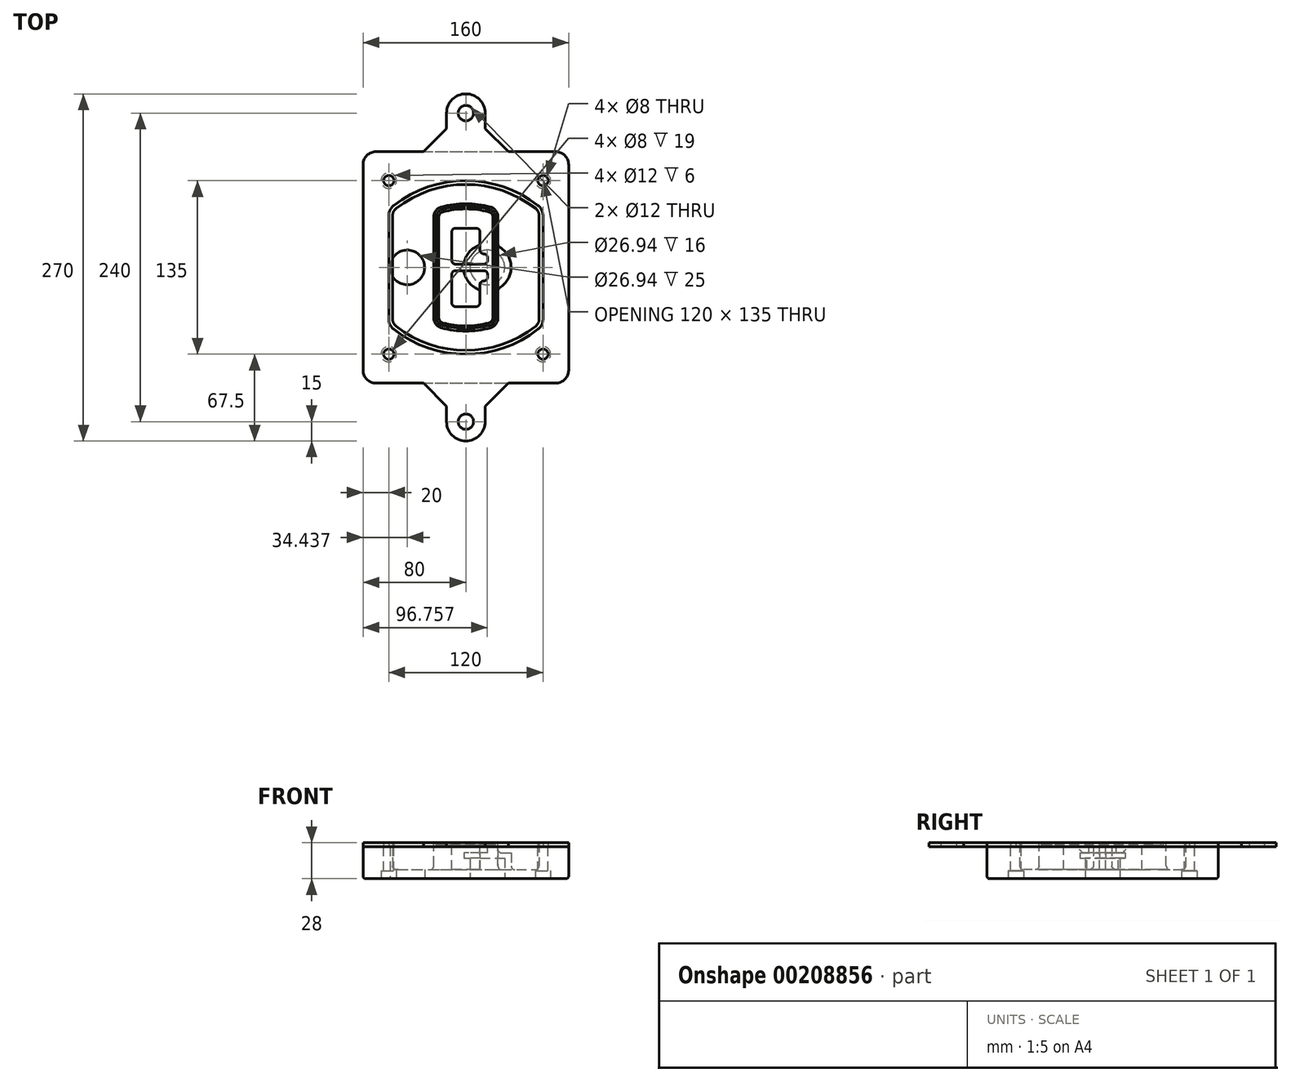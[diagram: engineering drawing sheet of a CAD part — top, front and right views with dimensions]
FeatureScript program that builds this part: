
annotation { "Feature Type Name" : "Feature", "Feature Type Description" : "" }
export const myFeature = defineFeature(function(context is Context, id is Id, definition is map)
    precondition{}
    {
        {
            var Q0;
            Q0=qCreatedBy(makeId("Top.planeOp"),FACE);
            var sketch = newSketch(context, id + "F0", { "sketchPlane" : qUnion([Q0])});
            skPoint(sketch, "E0.rect.middle", {"position": v(0, 0) * mm});
            skLineSegment(sketch, "E1.bottom", {"start": v(-70, -90) * mm, "end": v(70, -90) * mm});
            skLineSegment(sketch, "E1.top", {"start": v(-70, 90) * mm, "end": v(70, 90) * mm});
            skLineSegment(sketch, "E1.left", {"start": v(-80, -80) * mm, "end": v(-80, 80) * mm});
            skLineSegment(sketch, "E1.right", {"start": v(80, -80) * mm, "end": v(80, 80) * mm});
            skLineSegment(sketch, "E2", {"start": v(-80, 90) * mm, "end": v(80, -90) * mm, "construction": true});
            skLineSegment(sketch, "E3", {"start": v(80, 90) * mm, "end": v(-80, -90) * mm, "construction": true});
            skCircle(sketch, "E4", {"center": v(-60, 67.5) * mm, "radius": 4 * mm});
            skCircle(sketch, "E5", {"center": v(60, 67.5) * mm, "radius": 4 * mm});
            skCircle(sketch, "E6", {"center": v(60, -67.5) * mm, "radius": 4 * mm});
            skCircle(sketch, "E7", {"center": v(-60, -67.5) * mm, "radius": 4 * mm});
            skLineSegment(sketch, "E8", {"start": v(-60, 67.5) * mm, "end": v(60, 67.5) * mm, "construction": true});
            skLineSegment(sketch, "E9", {"start": v(60, 67.5) * mm, "end": v(60, -67.5) * mm, "construction": true});
            skLineSegment(sketch, "E10", {"start": v(60, -67.5) * mm, "end": v(-60, -67.5) * mm, "construction": true});
            skLineSegment(sketch, "E11", {"start": v(-60, -67.5) * mm, "end": v(-60, 67.5) * mm, "construction": true});
            skLineSegment(sketch, "E12", {"start": v(-60, 40.3) * mm, "end": v(-60, -40.3) * mm});
            skLineSegment(sketch, "E13", {"start": v(60, 40.3) * mm, "end": v(60, -40.3) * mm});
            skArc(sketch, "E14", {"start": v(56.15, 48.18) * mm, "mid": v(0, 67.5) * mm, "end": v(-56.15, 48.18) * mm});
            skArc(sketch, "E15", {"start": v(-56.15, -48.18) * mm, "mid": v(0, -67.5) * mm, "end": v(56.15, -48.18) * mm});
            skLineSegment(sketch, "E16", {"start": v(-60, 0) * mm, "end": v(60, 0) * mm, "construction": true});
            skPoint(sketch, "E17.visualSharp", {"position": v(-60, -45) * mm});
            skArc(sketch, "E17.filletArc", {"start": v(-60, -40.3) * mm, "mid": v(-58.99, -44.68) * mm, "end": v(-56.15, -48.18) * mm});
            skPoint(sketch, "E18.visualSharp", {"position": v(-60, 45) * mm});
            skArc(sketch, "E18.filletArc", {"start": v(-56.15, 48.18) * mm, "mid": v(-58.99, 44.68) * mm, "end": v(-60, 40.3) * mm});
            skPoint(sketch, "E19.visualSharp", {"position": v(60, 45) * mm});
            skArc(sketch, "E19.filletArc", {"start": v(60, 40.3) * mm, "mid": v(58.99, 44.68) * mm, "end": v(56.15, 48.18) * mm});
            skPoint(sketch, "E20.visualSharp", {"position": v(60, -45) * mm});
            skArc(sketch, "E20.filletArc", {"start": v(56.15, -48.18) * mm, "mid": v(58.99, -44.68) * mm, "end": v(60, -40.3) * mm});
            skPoint(sketch, "E21.visualSharp", {"position": v(-80, 90) * mm});
            skArc(sketch, "E21.filletArc", {"start": v(-70, 90) * mm, "mid": v(-77.07, 87.07) * mm, "end": v(-80, 80) * mm});
            skPoint(sketch, "E22.visualSharp", {"position": v(80, 90) * mm});
            skArc(sketch, "E22.filletArc", {"start": v(80, 80) * mm, "mid": v(77.07, 87.07) * mm, "end": v(70, 90) * mm});
            skPoint(sketch, "E23.visualSharp", {"position": v(80, -90) * mm});
            skArc(sketch, "E23.filletArc", {"start": v(70, -90) * mm, "mid": v(77.07, -87.07) * mm, "end": v(80, -80) * mm});
            skPoint(sketch, "E24.visualSharp", {"position": v(-80, -90) * mm});
            skArc(sketch, "E24.filletArc", {"start": v(-80, -80) * mm, "mid": v(-77.07, -87.07) * mm, "end": v(-70, -90) * mm});
            skArc(sketch, "E25.0", {"start": v(57, 40.3) * mm, "mid": v(56.3, 43.36) * mm, "end": v(54.3, 45.81) * mm});
            skLineSegment(sketch, "E25.1", {"start": v(57, 40.3) * mm, "end": v(57, -40.3) * mm});
            skArc(sketch, "E25.2", {"start": v(54.3, -45.81) * mm, "mid": v(56.3, -43.36) * mm, "end": v(57, -40.3) * mm});
            skArc(sketch, "E25.3", {"start": v(-54.3, -45.81) * mm, "mid": v(0, -64.5) * mm, "end": v(54.3, -45.81) * mm});
            skArc(sketch, "E25.4", {"start": v(-57, -40.3) * mm, "mid": v(-56.3, -43.36) * mm, "end": v(-54.3, -45.81) * mm});
            skArc(sketch, "E25.5", {"start": v(54.3, 45.81) * mm, "mid": v(0, 64.5) * mm, "end": v(-54.3, 45.81) * mm});
            skLineSegment(sketch, "E25.6", {"start": v(-57, 40.3) * mm, "end": v(-57, -40.3) * mm});
            skArc(sketch, "E25.7", {"start": v(-54.3, 45.81) * mm, "mid": v(-56.3, 43.36) * mm, "end": v(-57, 40.3) * mm});
            skArc(sketch, "E26.0", {"start": v(-58.62, 51.33) * mm, "mid": v(-62.58, 46.43) * mm, "end": v(-64, 40.3) * mm});
            skArc(sketch, "E26.1", {"start": v(58.62, 51.33) * mm, "mid": v(0, 71.5) * mm, "end": v(-58.62, 51.33) * mm});
            skArc(sketch, "E26.2", {"start": v(64, 40.3) * mm, "mid": v(62.58, 46.43) * mm, "end": v(58.62, 51.33) * mm});
            skLineSegment(sketch, "E26.3", {"start": v(64, 40.3) * mm, "end": v(64, -40.3) * mm});
            skArc(sketch, "E26.4", {"start": v(58.62, -51.33) * mm, "mid": v(62.58, -46.43) * mm, "end": v(64, -40.3) * mm});
            skLineSegment(sketch, "E26.5", {"start": v(-64, 40.3) * mm, "end": v(-64, -40.3) * mm});
            skArc(sketch, "E26.6", {"start": v(-58.62, -51.33) * mm, "mid": v(0, -71.5) * mm, "end": v(58.62, -51.33) * mm});
            skArc(sketch, "E26.7", {"start": v(-64, -40.3) * mm, "mid": v(-62.58, -46.43) * mm, "end": v(-58.62, -51.33) * mm});
            skSolve(sketch);
        }
        {
            var Q0;
            Q0=makeQuery(id+"F0.imprint","IMPRINT",FACE,{"disambiguationData":[TD([[makeQuery(id+"F0.imprint","IMPRINT",EDGE,{"derivedFrom":sQuery(id+"F0.wireOp",EDGE,"E1.bottom")}),1.0]])]});
            var Q1;
            Q1=makeQuery(id+"F0.imprint","IMPRINT",FACE,{"disambiguationData":[TD([[makeQuery(id+"F0.imprint","IMPRINT",EDGE,{"derivedFrom":sQuery(id+"F0.wireOp",EDGE,"E12")}),1.0]])]});
            var Q2;
            Q2=makeQuery(id+"F0.imprint","IMPRINT",FACE,{"disambiguationData":[TD([[makeQuery(id+"F0.imprint","IMPRINT",EDGE,{"derivedFrom":sQuery(id+"F0.wireOp",EDGE,"E25.0")}),1.0]])]});
            var Q3;
            Q3=makeQuery(id+"F0.imprint","IMPRINT",FACE,{"disambiguationData":[TD([[makeQuery(id+"F0.imprint","IMPRINT",EDGE,{"derivedFrom":sQuery(id+"F0.wireOp",EDGE,"E12")}),-1.0]])]});
            extrude(context, id + "F1", {"entities" : qUnion([Q0, Q1, Q2, Q3]), "oppositeDirection" : true, "depth" : 25 * mm});
        }
        {
            var Q0;
            Q0=makeQuery(id+"F0.imprint","IMPRINT",FACE,{"disambiguationData":[TD([[makeQuery(id+"F0.imprint","IMPRINT",EDGE,{"derivedFrom":sQuery(id+"F0.wireOp",EDGE,"E12")}),1.0]])]});
            extrude(context, id + "F2", {"entities" : qUnion([Q0]), "operationType" : NewBodyOperationType.ADD, "depth" : 3 * mm});
        }
        {
            var Q0;
            Q0=makeQuery(id+"F0.imprint","IMPRINT",FACE,{"disambiguationData":[TD([[makeQuery(id+"F0.imprint","IMPRINT",EDGE,{"derivedFrom":sQuery(id+"F0.wireOp",EDGE,"E25.0")}),1.0]])]});
            extrude(context, id + "F3", {"entities" : qUnion([Q0]), "operationType" : NewBodyOperationType.REMOVE, "oppositeDirection" : true, "depth" : 18 * mm});
        }
        {
            var Q0;
            Q0=makeQuery(id+"F2.opExtrude","CAP_FACE",FACE,{"disambiguationData":[OSD([sQuery(id+"F0.wireOp",EDGE,"E12"),sQuery(id+"F0.wireOp",EDGE,"E13"),sQuery(id+"F0.wireOp",EDGE,"E14"),sQuery(id+"F0.wireOp",EDGE,"E15"),sQuery(id+"F0.wireOp",EDGE,"E17.filletArc"),sQuery(id+"F0.wireOp",EDGE,"E18.filletArc"),sQuery(id+"F0.wireOp",EDGE,"E19.filletArc"),sQuery(id+"F0.wireOp",EDGE,"E20.filletArc"),sQuery(id+"F0.wireOp",EDGE,"E25.0"),sQuery(id+"F0.wireOp",EDGE,"E25.1"),sQuery(id+"F0.wireOp",EDGE,"E25.2"),sQuery(id+"F0.wireOp",EDGE,"E25.3"),sQuery(id+"F0.wireOp",EDGE,"E25.4"),sQuery(id+"F0.wireOp",EDGE,"E25.5"),sQuery(id+"F0.wireOp",EDGE,"E25.6"),sQuery(id+"F0.wireOp",EDGE,"E25.7")])],"isStart":false});
            var sketch = newSketch(context, id + "F4", { "sketchPlane" : qUnion([Q0])});
            skArc(sketch, "E27.0", {"start": v(-19.08, -46.97) * mm, "mid": v(0, -49.5) * mm, "end": v(19.08, -46.97) * mm});
            skArc(sketch, "E28.0", {"start": v(19.08, 46.97) * mm, "mid": v(0, 49.5) * mm, "end": v(-19.08, 46.97) * mm});
            skLineSegment(sketch, "E29", {"start": v(-25, 39.25) * mm, "end": v(-25, -39.25) * mm});
            skLineSegment(sketch, "E30", {"start": v(25, 39.25) * mm, "end": v(25, -39.25) * mm});
            skLineSegment(sketch, "E31", {"start": v(-25, 45.1) * mm, "end": v(25, 45.1) * mm, "construction": true});
            skLineSegment(sketch, "E32", {"start": v(-25, -45.1) * mm, "end": v(25, -45.1) * mm, "construction": true});
            skPoint(sketch, "E33.visualSharp", {"position": v(-25, 45.1) * mm});
            skArc(sketch, "E33.filletArc", {"start": v(-19.08, 46.97) * mm, "mid": v(-23.35, 44.11) * mm, "end": v(-25, 39.25) * mm});
            skPoint(sketch, "E34.visualSharp", {"position": v(25, 45.1) * mm});
            skArc(sketch, "E34.filletArc", {"start": v(25, 39.25) * mm, "mid": v(23.35, 44.11) * mm, "end": v(19.08, 46.97) * mm});
            skPoint(sketch, "E35.visualSharp", {"position": v(25, -45.1) * mm});
            skArc(sketch, "E35.filletArc", {"start": v(19.08, -46.97) * mm, "mid": v(23.35, -44.11) * mm, "end": v(25, -39.25) * mm});
            skPoint(sketch, "E36.visualSharp", {"position": v(-25, -45.1) * mm});
            skArc(sketch, "E36.filletArc", {"start": v(-25, -39.25) * mm, "mid": v(-23.35, -44.11) * mm, "end": v(-19.08, -46.97) * mm});
            skArc(sketch, "E37.0", {"start": v(54.3, 45.81) * mm, "mid": v(0, 64.5) * mm, "end": v(-54.3, 45.81) * mm});
            skArc(sketch, "E37.1", {"start": v(-54.3, 45.81) * mm, "mid": v(-56.3, 43.36) * mm, "end": v(-57, 40.3) * mm});
            skLineSegment(sketch, "E37.2", {"start": v(-57, 40.3) * mm, "end": v(-57, -40.3) * mm});
            skArc(sketch, "E37.3", {"start": v(-57, -40.3) * mm, "mid": v(-56.3, -43.36) * mm, "end": v(-54.3, -45.81) * mm});
            skArc(sketch, "E37.4", {"start": v(-54.3, -45.81) * mm, "mid": v(0, -64.5) * mm, "end": v(54.3, -45.81) * mm});
            skArc(sketch, "E37.5", {"start": v(54.3, -45.81) * mm, "mid": v(56.3, -43.36) * mm, "end": v(57, -40.3) * mm});
            skLineSegment(sketch, "E37.6", {"start": v(57, 40.3) * mm, "end": v(57, -40.3) * mm});
            skArc(sketch, "E37.7", {"start": v(57, 40.3) * mm, "mid": v(56.3, 43.36) * mm, "end": v(54.3, 45.81) * mm});
            skLineSegment(sketch, "E38.0", {"start": v(23, 39.25) * mm, "end": v(23, -39.25) * mm});
            skArc(sketch, "E38.1", {"start": v(18.56, -45.04) * mm, "mid": v(21.76, -42.9) * mm, "end": v(23, -39.25) * mm});
            skArc(sketch, "E38.2", {"start": v(-18.56, -45.04) * mm, "mid": v(0, -47.5) * mm, "end": v(18.56, -45.04) * mm});
            skArc(sketch, "E38.3", {"start": v(-23, -39.25) * mm, "mid": v(-21.76, -42.9) * mm, "end": v(-18.56, -45.04) * mm});
            skLineSegment(sketch, "E38.4", {"start": v(-23, 39.25) * mm, "end": v(-23, -39.25) * mm});
            skArc(sketch, "E38.5", {"start": v(23, 39.25) * mm, "mid": v(21.76, 42.9) * mm, "end": v(18.56, 45.04) * mm});
            skArc(sketch, "E38.6", {"start": v(-18.56, 45.04) * mm, "mid": v(-21.76, 42.9) * mm, "end": v(-23, 39.25) * mm});
            skArc(sketch, "E38.7", {"start": v(18.56, 45.04) * mm, "mid": v(0, 47.5) * mm, "end": v(-18.56, 45.04) * mm});
            skArc(sketch, "E39.0", {"start": v(21, 39.25) * mm, "mid": v(20.18, 41.68) * mm, "end": v(18.04, 43.1) * mm});
            skLineSegment(sketch, "E39.1", {"start": v(21, 39.25) * mm, "end": v(21, -39.25) * mm});
            skArc(sketch, "E39.2", {"start": v(18.04, -43.1) * mm, "mid": v(20.18, -41.68) * mm, "end": v(21, -39.25) * mm});
            skArc(sketch, "E39.3", {"start": v(-18.04, -43.1) * mm, "mid": v(0, -45.5) * mm, "end": v(18.04, -43.1) * mm});
            skArc(sketch, "E39.4", {"start": v(-21, -39.25) * mm, "mid": v(-20.18, -41.68) * mm, "end": v(-18.04, -43.1) * mm});
            skArc(sketch, "E39.5", {"start": v(18.04, 43.1) * mm, "mid": v(0, 45.5) * mm, "end": v(-18.04, 43.1) * mm});
            skLineSegment(sketch, "E39.6", {"start": v(-21, 39.25) * mm, "end": v(-21, -39.25) * mm});
            skArc(sketch, "E39.7", {"start": v(-18.04, 43.1) * mm, "mid": v(-20.18, 41.68) * mm, "end": v(-21, 39.25) * mm});
            skLineSegment(sketch, "E40", {"start": v(-25, 0) * mm, "end": v(25, 0) * mm, "construction": true});
            skLineSegment(sketch, "E41", {"start": v(-11, 5.5) * mm, "end": v(-11, 27.5) * mm});
            skLineSegment(sketch, "E42", {"start": v(-8, 30.5) * mm, "end": v(8, 30.5) * mm});
            skLineSegment(sketch, "E43", {"start": v(11, 27.5) * mm, "end": v(11, 13.5) * mm});
            skLineSegment(sketch, "E44", {"start": v(14, 10.5) * mm, "end": v(14, 10.5) * mm});
            skLineSegment(sketch, "E45", {"start": v(17, 7.5) * mm, "end": v(17, 5.5) * mm});
            skLineSegment(sketch, "E46", {"start": v(14, 2.5) * mm, "end": v(-8, 2.5) * mm});
            skPoint(sketch, "E47.visualSharp", {"position": v(-11, 30.5) * mm});
            skArc(sketch, "E47.filletArc", {"start": v(-8, 30.5) * mm, "mid": v(-10.12, 29.62) * mm, "end": v(-11, 27.5) * mm});
            skPoint(sketch, "E48.visualSharp", {"position": v(11, 30.5) * mm});
            skArc(sketch, "E48.filletArc", {"start": v(11, 27.5) * mm, "mid": v(10.12, 29.62) * mm, "end": v(8, 30.5) * mm});
            skPoint(sketch, "E49.visualSharp", {"position": v(11, 10.5) * mm});
            skArc(sketch, "E49.filletArc", {"start": v(11, 13.5) * mm, "mid": v(11.88, 11.38) * mm, "end": v(14, 10.5) * mm});
            skPoint(sketch, "E50.visualSharp", {"position": v(17, 10.5) * mm});
            skArc(sketch, "E50.filletArc", {"start": v(17, 7.5) * mm, "mid": v(16.12, 9.62) * mm, "end": v(14, 10.5) * mm});
            skPoint(sketch, "E51.visualSharp", {"position": v(17, 2.5) * mm});
            skArc(sketch, "E51.filletArc", {"start": v(14, 2.5) * mm, "mid": v(16.12, 3.38) * mm, "end": v(17, 5.5) * mm});
            skPoint(sketch, "E52.visualSharp", {"position": v(-11, 2.5) * mm});
            skArc(sketch, "E52.filletArc", {"start": v(-11, 5.5) * mm, "mid": v(-10.12, 3.38) * mm, "end": v(-8, 2.5) * mm});
            skLineSegment(sketch, "E53.0.MirrorCS", {"start": v(14, -2.5) * mm, "end": v(-8, -2.5) * mm});
            skArc(sketch, "E54.0.MirrorCS", {"start": v(-11, -5.5) * mm, "mid": v(-10.12, -3.38) * mm, "end": v(-8, -2.5) * mm});
            skLineSegment(sketch, "E55.0.MirrorCS", {"start": v(-11, -5.5) * mm, "end": v(-11, -27.5) * mm});
            skArc(sketch, "E56.0.MirrorCS", {"start": v(-8, -30.5) * mm, "mid": v(-10.12, -29.62) * mm, "end": v(-11, -27.5) * mm});
            skLineSegment(sketch, "E57.0.MirrorCS", {"start": v(-8, -30.5) * mm, "end": v(8, -30.5) * mm});
            skArc(sketch, "E58.0.MirrorCS", {"start": v(11, -27.5) * mm, "mid": v(10.12, -29.62) * mm, "end": v(8, -30.5) * mm});
            skLineSegment(sketch, "E59.0.MirrorCS", {"start": v(11, -27.5) * mm, "end": v(11, -13.5) * mm});
            skArc(sketch, "E60.0.MirrorCS", {"start": v(11, -13.5) * mm, "mid": v(11.88, -11.38) * mm, "end": v(14, -10.5) * mm});
            skArc(sketch, "E61.0.MirrorCS", {"start": v(17, -7.5) * mm, "mid": v(16.12, -9.62) * mm, "end": v(14, -10.5) * mm});
            skLineSegment(sketch, "E62.0.MirrorCS", {"start": v(17, -7.5) * mm, "end": v(17, -5.5) * mm});
            skArc(sketch, "E63.0.MirrorCS", {"start": v(14, -2.5) * mm, "mid": v(16.12, -3.38) * mm, "end": v(17, -5.5) * mm});
            skSolve(sketch);
        }
        {
            var Q0;
            Q0=makeQuery(id+"F4.imprint","IMPRINT",FACE,{"disambiguationData":[TD([[makeQuery(id+"F4.imprint","IMPRINT",EDGE,{"derivedFrom":sQuery(id+"F4.wireOp",EDGE,"E27.0")}),1.0]])]});
            var Q1;
            Q1=makeQuery(id+"F4.imprint","IMPRINT",FACE,{"disambiguationData":[TD([[makeQuery(id+"F4.imprint","IMPRINT",EDGE,{"derivedFrom":sQuery(id+"F4.wireOp",EDGE,"E38.0")}),-1.0]])]});
            var Q2;
            Q2=makeQuery(id+"F4.imprint","IMPRINT",FACE,{"disambiguationData":[TD([[makeQuery(id+"F4.imprint","IMPRINT",EDGE,{"derivedFrom":sQuery(id+"F4.wireOp",EDGE,"E39.0")}),1.0]])]});
            extrude(context, id + "F5", {"entities" : qUnion([Q0, Q1, Q2]), "operationType" : NewBodyOperationType.ADD, "endBound" : BoundingType.UP_TO_NEXT, "oppositeDirection" : true, "depth" : 25 * mm});
        }
        {
            var Q0;
            Q0=makeQuery(id+"F4.imprint","IMPRINT",FACE,{"disambiguationData":[TD([[makeQuery(id+"F4.imprint","IMPRINT",EDGE,{"derivedFrom":sQuery(id+"F4.wireOp",EDGE,"E38.0")}),-1.0]])]});
            extrude(context, id + "F6", {"entities" : qUnion([Q0]), "operationType" : NewBodyOperationType.REMOVE, "oppositeDirection" : true, "depth" : 2 * mm});
        }
        {
            var Q0;
            Q0=makeQuery(id+"F1.opExtrude","CAP_FACE",FACE,{"disambiguationData":[OSD([sQuery(id+"F0.wireOp",EDGE,"E1.bottom"),sQuery(id+"F0.wireOp",EDGE,"E1.top"),sQuery(id+"F0.wireOp",EDGE,"E1.left"),sQuery(id+"F0.wireOp",EDGE,"E1.right"),sQuery(id+"F0.wireOp",EDGE,"E4"),sQuery(id+"F0.wireOp",EDGE,"E5"),sQuery(id+"F0.wireOp",EDGE,"E6"),sQuery(id+"F0.wireOp",EDGE,"E7"),sQuery(id+"F0.wireOp",EDGE,"E21.filletArc"),sQuery(id+"F0.wireOp",EDGE,"E22.filletArc"),sQuery(id+"F0.wireOp",EDGE,"E23.filletArc"),sQuery(id+"F0.wireOp",EDGE,"E24.filletArc")])],"isStart":false});
            var sketch = newSketch(context, id + "F7", { "sketchPlane" : qUnion([Q0])});
            skCircle(sketch, "E64", {"center": v(16.76, 0) * mm, "radius": 13.47 * mm});
            skCircle(sketch, "E65", {"center": v(-45.56, 0) * mm, "radius": 13.47 * mm});
            skLineSegment(sketch, "E66", {"start": v(80, 0) * mm, "end": v(-80, 0) * mm});
            skCircle(sketch, "E67", {"center": v(16.76, 0) * mm, "radius": 18.47 * mm});
            skCircle(sketch, "E68", {"center": v(60, -67.5) * mm, "radius": 6 * mm});
            skCircle(sketch, "E69", {"center": v(-60, -67.5) * mm, "radius": 6 * mm});
            skCircle(sketch, "E70", {"center": v(-60, 67.5) * mm, "radius": 6 * mm});
            skCircle(sketch, "E71", {"center": v(60, 67.5) * mm, "radius": 6 * mm});
            skSolve(sketch);
        }
        {
            var Q0;
            {var subQ1=sQuery(id+"F7.wireOp",EDGE,"E66");var subQ4=sQuery(id+"F7.wireOp",EDGE,"E64");var subQ6=makeQuery(id+"F7.imprint","INTERSECT",VERTEX,{"disambiguationData":[OD(0.0)],"derivedFrom":[subQ4,subQ1]});Q0=makeQuery(id+"F7.imprint","IMPRINT",FACE,{"disambiguationData":[TD([[makeQuery(id+"F7.imprint","IMPRINT",EDGE,{"disambiguationData":[TD([[subQ6,-1.0]])],"derivedFrom":subQ4}),-1.0]])]});}
            var Q1;
            {var subQ0=sQuery(id+"F7.wireOp",EDGE,"E66");var subQ1=sQuery(id+"F7.wireOp",EDGE,"E64");var subQ3=makeQuery(id+"F7.imprint","INTERSECT",VERTEX,{"disambiguationData":[OD(0.0)],"derivedFrom":[subQ1,subQ0]});Q1=makeQuery(id+"F7.imprint","IMPRINT",FACE,{"disambiguationData":[TD([[makeQuery(id+"F7.imprint","IMPRINT",EDGE,{"disambiguationData":[TD([[subQ3,-1.0]])],"derivedFrom":subQ1}),1.0]])]});}
            var Q2;
            {var subQ0=sQuery(id+"F7.wireOp",EDGE,"E66");var subQ1=sQuery(id+"F7.wireOp",EDGE,"E64");var subQ3=makeQuery(id+"F7.imprint","INTERSECT",VERTEX,{"disambiguationData":[OD(0.0)],"derivedFrom":[subQ1,subQ0]});Q2=makeQuery(id+"F7.imprint","IMPRINT",FACE,{"disambiguationData":[TD([[makeQuery(id+"F7.imprint","IMPRINT",EDGE,{"disambiguationData":[TD([[subQ3,1.0]])],"derivedFrom":subQ1}),1.0]])]});}
            var Q3;
            {var subQ1=sQuery(id+"F7.wireOp",EDGE,"E66");var subQ4=sQuery(id+"F7.wireOp",EDGE,"E64");var subQ6=makeQuery(id+"F7.imprint","INTERSECT",VERTEX,{"disambiguationData":[OD(0.0)],"derivedFrom":[subQ4,subQ1]});Q3=makeQuery(id+"F7.imprint","IMPRINT",FACE,{"disambiguationData":[TD([[makeQuery(id+"F7.imprint","IMPRINT",EDGE,{"disambiguationData":[TD([[subQ6,1.0]])],"derivedFrom":subQ4}),-1.0]])]});}
            extrude(context, id + "F8", {"entities" : qUnion([Q0, Q1, Q2, Q3]), "operationType" : NewBodyOperationType.ADD, "oppositeDirection" : true, "depth" : 20 * mm});
        }
        {
            var Q0;
            {var subQ0=sQuery(id+"F7.wireOp",EDGE,"E66");var subQ1=sQuery(id+"F7.wireOp",EDGE,"E64");var subQ3=makeQuery(id+"F7.imprint","INTERSECT",VERTEX,{"disambiguationData":[OD(0.0)],"derivedFrom":[subQ1,subQ0]});Q0=makeQuery(id+"F7.imprint","IMPRINT",FACE,{"disambiguationData":[TD([[makeQuery(id+"F7.imprint","IMPRINT",EDGE,{"disambiguationData":[TD([[subQ3,-1.0]])],"derivedFrom":subQ1}),1.0]])]});}
            var Q1;
            {var subQ0=sQuery(id+"F7.wireOp",EDGE,"E66");var subQ1=sQuery(id+"F7.wireOp",EDGE,"E64");var subQ3=makeQuery(id+"F7.imprint","INTERSECT",VERTEX,{"disambiguationData":[OD(0.0)],"derivedFrom":[subQ1,subQ0]});Q1=makeQuery(id+"F7.imprint","IMPRINT",FACE,{"disambiguationData":[TD([[makeQuery(id+"F7.imprint","IMPRINT",EDGE,{"disambiguationData":[TD([[subQ3,1.0]])],"derivedFrom":subQ1}),1.0]])]});}
            extrude(context, id + "F9", {"entities" : qUnion([Q0, Q1]), "operationType" : NewBodyOperationType.REMOVE, "oppositeDirection" : true, "depth" : 16 * mm});
        }
        {
            var Q0;
            {var subQ0=sQuery(id+"F7.wireOp",EDGE,"E66");var subQ1=sQuery(id+"F7.wireOp",EDGE,"E65");var subQ3=makeQuery(id+"F7.imprint","INTERSECT",VERTEX,{"disambiguationData":[OD(0.0)],"derivedFrom":[subQ1,subQ0]});Q0=makeQuery(id+"F7.imprint","IMPRINT",FACE,{"disambiguationData":[TD([[makeQuery(id+"F7.imprint","IMPRINT",EDGE,{"disambiguationData":[TD([[subQ3,-1.0]])],"derivedFrom":subQ1}),1.0]])]});}
            var Q1;
            {var subQ0=sQuery(id+"F7.wireOp",EDGE,"E66");var subQ1=sQuery(id+"F7.wireOp",EDGE,"E65");var subQ3=makeQuery(id+"F7.imprint","INTERSECT",VERTEX,{"disambiguationData":[OD(0.0)],"derivedFrom":[subQ1,subQ0]});Q1=makeQuery(id+"F7.imprint","IMPRINT",FACE,{"disambiguationData":[TD([[makeQuery(id+"F7.imprint","IMPRINT",EDGE,{"disambiguationData":[TD([[subQ3,1.0]])],"derivedFrom":subQ1}),1.0]])]});}
            extrude(context, id + "F10", {"entities" : qUnion([Q0, Q1]), "operationType" : NewBodyOperationType.REMOVE, "oppositeDirection" : true, "depth" : 25 * mm});
        }
        {
            var Q0;
            Q0=makeQuery(id+"F7.imprint","IMPRINT",FACE,{"disambiguationData":[TD([[makeQuery(id+"F7.imprint","IMPRINT",EDGE,{"derivedFrom":sQuery(id+"F7.wireOp",EDGE,"E68")}),1.0]])]});
            var Q1;
            Q1=makeQuery(id+"F7.imprint","IMPRINT",FACE,{"disambiguationData":[TD([[makeQuery(id+"F7.imprint","IMPRINT",EDGE,{"derivedFrom":makeQuery(id+"F1.opExtrude","CAP_EDGE",EDGE,{"disambiguationData":[OSD([sQuery(id+"F0.wireOp",EDGE,"E5")])],"isStart":false})}),-1.0]])]});
            var Q2;
            Q2=makeQuery(id+"F7.imprint","IMPRINT",FACE,{"disambiguationData":[TD([[makeQuery(id+"F7.imprint","IMPRINT",EDGE,{"derivedFrom":sQuery(id+"F7.wireOp",EDGE,"E69")}),1.0]])]});
            var Q3;
            Q3=makeQuery(id+"F7.imprint","IMPRINT",FACE,{"disambiguationData":[TD([[makeQuery(id+"F7.imprint","IMPRINT",EDGE,{"derivedFrom":makeQuery(id+"F1.opExtrude","CAP_EDGE",EDGE,{"disambiguationData":[OSD([sQuery(id+"F0.wireOp",EDGE,"E4")])],"isStart":false})}),-1.0]])]});
            var Q4;
            Q4=makeQuery(id+"F7.imprint","IMPRINT",FACE,{"disambiguationData":[TD([[makeQuery(id+"F7.imprint","IMPRINT",EDGE,{"derivedFrom":sQuery(id+"F7.wireOp",EDGE,"E70")}),1.0]])]});
            var Q5;
            Q5=makeQuery(id+"F7.imprint","IMPRINT",FACE,{"disambiguationData":[TD([[makeQuery(id+"F7.imprint","IMPRINT",EDGE,{"derivedFrom":makeQuery(id+"F1.opExtrude","CAP_EDGE",EDGE,{"disambiguationData":[OSD([sQuery(id+"F0.wireOp",EDGE,"E7")])],"isStart":false})}),-1.0]])]});
            var Q6;
            Q6=makeQuery(id+"F7.imprint","IMPRINT",FACE,{"disambiguationData":[TD([[makeQuery(id+"F7.imprint","IMPRINT",EDGE,{"derivedFrom":sQuery(id+"F7.wireOp",EDGE,"E71")}),1.0]])]});
            var Q7;
            Q7=makeQuery(id+"F7.imprint","IMPRINT",FACE,{"disambiguationData":[TD([[makeQuery(id+"F7.imprint","IMPRINT",EDGE,{"derivedFrom":makeQuery(id+"F1.opExtrude","CAP_EDGE",EDGE,{"disambiguationData":[OSD([sQuery(id+"F0.wireOp",EDGE,"E6")])],"isStart":false})}),-1.0]])]});
            extrude(context, id + "F11", {"entities" : qUnion([Q0, Q1, Q2, Q3, Q4, Q5, Q6, Q7]), "operationType" : NewBodyOperationType.REMOVE, "oppositeDirection" : true, "depth" : 6 * mm});
        }
        {
            var Q0;
            Q0=makeQuery(id+"F9.boolean.opBoolean","COPY",FACE,{"derivedFrom":makeQuery(id+"F9.opExtrude","CAP_FACE",FACE,{"disambiguationData":[OSD([sQuery(id+"F7.wireOp",EDGE,"E64")])],"isStart":false})});
            var sketch = newSketch(context, id + "F12", { "sketchPlane" : qUnion([Q0])});
            skArc(sketch, "E72.0", {"start": v(11, 17.55) * mm, "mid": v(2.57, 11.82) * mm, "end": v(-1.54, 2.5) * mm});
            skArc(sketch, "E72.1", {"start": v(-1.54, -2.5) * mm, "mid": v(2.57, -11.82) * mm, "end": v(11, -17.55) * mm});
            skLineSegment(sketch, "E73", {"start": v(-1.54, -2.5) * mm, "end": v(14, -2.5) * mm});
            skLineSegment(sketch, "E74.0", {"start": v(14, 2.5) * mm, "end": v(-1.54, 2.5) * mm});
            skArc(sketch, "E74.1", {"start": v(14, 2.5) * mm, "mid": v(16.12, 3.38) * mm, "end": v(17, 5.5) * mm});
            skLineSegment(sketch, "E74.2", {"start": v(17, 7.5) * mm, "end": v(17, 5.5) * mm});
            skArc(sketch, "E74.3", {"start": v(17, 7.5) * mm, "mid": v(16.12, 9.62) * mm, "end": v(14, 10.5) * mm});
            skArc(sketch, "E74.4", {"start": v(11, 13.5) * mm, "mid": v(11.88, 11.38) * mm, "end": v(14, 10.5) * mm});
            skLineSegment(sketch, "E74.5", {"start": v(11, 17.55) * mm, "end": v(11, 13.5) * mm});
            skLineSegment(sketch, "E74.7", {"start": v(14, -2.5) * mm, "end": v(-1.54, -2.5) * mm});
            skArc(sketch, "E74.8", {"start": v(14, -2.5) * mm, "mid": v(16.12, -3.38) * mm, "end": v(17, -5.5) * mm});
            skLineSegment(sketch, "E74.9", {"start": v(17, -7.5) * mm, "end": v(17, -5.5) * mm});
            skArc(sketch, "E74.10", {"start": v(17, -7.5) * mm, "mid": v(16.12, -9.62) * mm, "end": v(14, -10.5) * mm});
            skArc(sketch, "E74.11", {"start": v(11, -13.5) * mm, "mid": v(11.88, -11.38) * mm, "end": v(14, -10.5) * mm});
            skLineSegment(sketch, "E74.12", {"start": v(11, -17.55) * mm, "end": v(11, -13.5) * mm});
            skPoint(sketch, "E75.orphan", {"position": v(11, -27.5) * mm});
            skPoint(sketch, "E76.orphan", {"position": v(-8, -2.5) * mm});
            skPoint(sketch, "E77.orphan", {"position": v(-8, 2.5) * mm});
            skPoint(sketch, "E78.orphan", {"position": v(11, 27.5) * mm});
            skSolve(sketch);
        }
        {
            var Q0;
            {var subQ7=sQuery(id+"F12.wireOp",EDGE,"E72.0");var subQ14=sQuery(id+"F12.wireOp",EDGE,"E72.1");var subQ16=sQuery(id+"F12.wireOp",EDGE,"E74.1");var subQ18=sQuery(id+"F12.wireOp",EDGE,"E74.8");Q0=qUnion([makeQuery(id+"F12.imprint","IMPRINT",FACE,{"disambiguationData":[TD([[makeQuery(id+"F12.imprint","IMPRINT",EDGE,{"derivedFrom":subQ7}),1.0]])]}),makeQuery(id+"F12.imprint","IMPRINT",FACE,{"disambiguationData":[TD([[makeQuery(id+"F12.imprint","IMPRINT",EDGE,{"derivedFrom":subQ14}),1.0]])]}),makeQuery(id+"F12.imprint","IMPRINT",FACE,{"disambiguationData":[TD([[makeQuery(id+"F12.imprint","IMPRINT",EDGE,{"derivedFrom":subQ16}),1.0]])]}),makeQuery(id+"F12.imprint","IMPRINT",FACE,{"disambiguationData":[TD([[makeQuery(id+"F12.imprint","IMPRINT",EDGE,{"derivedFrom":subQ18}),-1.0]])]})]);}
            var Q1;
            Q1=makeQuery(id+"F5.boolean.opBoolean","SPLIT",FACE,{"disambiguationData":[TD([makeQuery(id+"F5.opExtrude","SWEPT_FACE",FACE,{"disambiguationData":[OSD([sQuery(id+"F4.wireOp",EDGE,"E41")])]})])],"derivedFrom":makeQuery(id+"F3.boolean.opBoolean","COPY",FACE,{"derivedFrom":makeQuery(id+"F3.opExtrude","CAP_FACE",FACE,{"disambiguationData":[OSD([sQuery(id+"F0.wireOp",EDGE,"E25.0"),sQuery(id+"F0.wireOp",EDGE,"E25.1"),sQuery(id+"F0.wireOp",EDGE,"E25.2"),sQuery(id+"F0.wireOp",EDGE,"E25.3"),sQuery(id+"F0.wireOp",EDGE,"E25.4"),sQuery(id+"F0.wireOp",EDGE,"E25.5"),sQuery(id+"F0.wireOp",EDGE,"E25.6"),sQuery(id+"F0.wireOp",EDGE,"E25.7")])],"isStart":false})})});
            extrude(context, id + "F13", {"entities" : qUnion([Q0]), "operationType" : NewBodyOperationType.REMOVE, "endBound" : BoundingType.UP_TO_SURFACE, "endBoundEntityFace" : qUnion([Q1]), "depth" : 25 * mm});
        }
        {
            var Q0;
            Q0=makeQuery(id+"F3.boolean.opBoolean","COPY",EDGE,{"derivedFrom":makeQuery(id+"F3.opExtrude","CAP_EDGE",EDGE,{"disambiguationData":[OSD([sQuery(id+"F0.wireOp",EDGE,"E25.6")])],"isStart":false})});
            var Q1;
            Q1=makeQuery(id+"F8.boolean.opBoolean","INTERSECT",EDGE,{"derivedFrom":[makeQuery(id+"F5.opExtrude","SWEPT_FACE",FACE,{"disambiguationData":[OSD([sQuery(id+"F4.wireOp",EDGE,"E30")])]}),makeQuery(id+"F8.opExtrude","CAP_FACE",FACE,{"disambiguationData":[OSD([sQuery(id+"F7.wireOp",EDGE,"E67")])],"isStart":false})]});
            var Q2;
            Q2=makeQuery(id+"F8.boolean.opBoolean","INTERSECT",EDGE,{"disambiguationData":[OD(1.0)],"derivedFrom":[makeQuery(id+"F5.opExtrude","SWEPT_FACE",FACE,{"disambiguationData":[OSD([sQuery(id+"F4.wireOp",EDGE,"E30")])]}),makeQuery(id+"F8.opExtrude","SWEPT_FACE",FACE,{"disambiguationData":[OSD([sQuery(id+"F7.wireOp",EDGE,"E67")])]})]});
            var Q3;
            {var subQ0=sQuery(id+"F4.wireOp",EDGE,"E30");Q3=makeQuery(id+"F8.boolean.opBoolean","SPLIT",EDGE,{"disambiguationData":[TD([makeQuery(id+"F5.opExtrude","SWEPT_FACE",FACE,{"disambiguationData":[OSD([sQuery(id+"F4.wireOp",EDGE,"E35.filletArc")])]})])],"derivedFrom":makeQuery(id+"F5.opExtrude","CAP_EDGE",EDGE,{"disambiguationData":[OSD([subQ0])],"isStart":false})});}
            var Q4;
            {var subQ0=sQuery(id+"F0.wireOp",EDGE,"E25.7");var subQ1=sQuery(id+"F0.wireOp",EDGE,"E25.1");var subQ2=sQuery(id+"F0.wireOp",EDGE,"E25.6");var subQ3=sQuery(id+"F0.wireOp",EDGE,"E25.5");var subQ4=sQuery(id+"F0.wireOp",EDGE,"E25.4");var subQ5=sQuery(id+"F0.wireOp",EDGE,"E25.0");var subQ6=sQuery(id+"F0.wireOp",EDGE,"E25.2");var subQ7=sQuery(id+"F0.wireOp",EDGE,"E25.3");Q4=makeQuery(id+"F8.boolean.opBoolean","INTERSECT",EDGE,{"derivedFrom":[makeQuery(id+"F5.boolean.opBoolean","SPLIT",FACE,{"disambiguationData":[TD([makeQuery(id+"F2.opExtrude","SWEPT_FACE",FACE,{"disambiguationData":[OSD([subQ5])]})])],"derivedFrom":makeQuery(id+"F3.boolean.opBoolean","COPY",FACE,{"derivedFrom":makeQuery(id+"F3.opExtrude","CAP_FACE",FACE,{"disambiguationData":[OSD([subQ5,subQ1,subQ6,subQ7,subQ4,subQ3,subQ2,subQ0])],"isStart":false})})}),makeQuery(id+"F8.opExtrude","SWEPT_FACE",FACE,{"disambiguationData":[OSD([sQuery(id+"F7.wireOp",EDGE,"E67")])]})]});}
            var Q5;
            Q5=makeQuery(id+"F8.boolean.opBoolean","INTERSECT",EDGE,{"disambiguationData":[OD(0.0)],"derivedFrom":[makeQuery(id+"F5.opExtrude","SWEPT_FACE",FACE,{"disambiguationData":[OSD([sQuery(id+"F4.wireOp",EDGE,"E30")])]}),makeQuery(id+"F8.opExtrude","SWEPT_FACE",FACE,{"disambiguationData":[OSD([sQuery(id+"F7.wireOp",EDGE,"E67")])]})]});
            fillet(context, id + "F14", {"entities" : qUnion([Q0, Q1, Q2, Q3, Q4, Q5]), "radius" : 3 * mm, "tangentPropagation" : true, "allowEdgeOverflow" : false});
        }
        {
            var Q0;
            Q0=makeQuery(id+"F1.opExtrude","CAP_EDGE",EDGE,{"disambiguationData":[OSD([sQuery(id+"F0.wireOp",EDGE,"E1.bottom")])],"isStart":false});
            fillet(context, id + "F15", {"entities" : qUnion([Q0]), "radius" : 2 * mm, "tangentPropagation" : true, "allowEdgeOverflow" : false});
        }
        {
            var Q0;
            {var subQ0=sQuery(id+"F0.wireOp",EDGE,"E22.filletArc");var subQ1=sQuery(id+"F0.wireOp",EDGE,"E7");var subQ2=sQuery(id+"F0.wireOp",EDGE,"E6");var subQ3=sQuery(id+"F0.wireOp",EDGE,"E5");var subQ4=sQuery(id+"F0.wireOp",EDGE,"E4");var subQ5=sQuery(id+"F0.wireOp",EDGE,"E1.bottom");var subQ6=sQuery(id+"F0.wireOp",EDGE,"E21.filletArc");var subQ7=sQuery(id+"F0.wireOp",EDGE,"E1.top");var subQ8=sQuery(id+"F0.wireOp",EDGE,"E1.left");var subQ9=sQuery(id+"F0.wireOp",EDGE,"E1.right");var subQ10=sQuery(id+"F0.wireOp",EDGE,"E23.filletArc");var subQ11=sQuery(id+"F0.wireOp",EDGE,"E24.filletArc");Q0=makeQuery(id+"F2.boolean.opBoolean","SPLIT",FACE,{"disambiguationData":[TD([makeQuery(id+"F1.opExtrude","SWEPT_FACE",FACE,{"disambiguationData":[OSD([subQ5])]})])],"derivedFrom":makeQuery(id+"F1.opExtrude","CAP_FACE",FACE,{"disambiguationData":[OSD([subQ5,subQ7,subQ8,subQ9,subQ4,subQ3,subQ2,subQ1,subQ6,subQ0,subQ10,subQ11])],"isStart":true})});}
            var sketch = newSketch(context, id + "F16", { "sketchPlane" : qUnion([Q0])});
            skArc(sketch, "E79.0", {"start": v(-80, -80) * mm, "mid": v(-77.07, -87.07) * mm, "end": v(-70, -90) * mm});
            skLineSegment(sketch, "E79.1", {"start": v(-70, -90) * mm, "end": v(70, -90) * mm});
            skLineSegment(sketch, "E79.2", {"start": v(-80, -80) * mm, "end": v(-80, 80) * mm});
            skArc(sketch, "E79.3", {"start": v(-70, 90) * mm, "mid": v(-77.07, 87.07) * mm, "end": v(-80, 80) * mm});
            skLineSegment(sketch, "E79.4", {"start": v(-70, 90) * mm, "end": v(70, 90) * mm});
            skArc(sketch, "E79.5", {"start": v(80, 80) * mm, "mid": v(77.07, 87.07) * mm, "end": v(70, 90) * mm});
            skLineSegment(sketch, "E79.6", {"start": v(80, -80) * mm, "end": v(80, 80) * mm});
            skArc(sketch, "E79.7", {"start": v(70, -90) * mm, "mid": v(77.07, -87.07) * mm, "end": v(80, -80) * mm});
            skCircle(sketch, "E79.8", {"center": v(60, -67.5) * mm, "radius": 4 * mm});
            skCircle(sketch, "E79.9", {"center": v(60, 67.5) * mm, "radius": 4 * mm});
            skCircle(sketch, "E79.10", {"center": v(-60, 67.5) * mm, "radius": 4 * mm});
            skCircle(sketch, "E79.11", {"center": v(-60, -67.5) * mm, "radius": 4 * mm});
            skArc(sketch, "E79.12", {"start": v(-56.15, -48.18) * mm, "mid": v(0, -67.5) * mm, "end": v(56.15, -48.18) * mm});
            skArc(sketch, "E79.13", {"start": v(56.15, -48.18) * mm, "mid": v(58.99, -44.68) * mm, "end": v(60, -40.3) * mm});
            skLineSegment(sketch, "E79.14", {"start": v(60, 40.3) * mm, "end": v(60, -40.3) * mm});
            skArc(sketch, "E79.15", {"start": v(60, 40.3) * mm, "mid": v(58.99, 44.68) * mm, "end": v(56.15, 48.18) * mm});
            skArc(sketch, "E79.16", {"start": v(56.15, 48.18) * mm, "mid": v(0, 67.5) * mm, "end": v(-56.15, 48.18) * mm});
            skArc(sketch, "E79.17", {"start": v(-56.15, 48.18) * mm, "mid": v(-58.99, 44.68) * mm, "end": v(-60, 40.3) * mm});
            skLineSegment(sketch, "E79.18", {"start": v(-60, 40.3) * mm, "end": v(-60, -40.3) * mm});
            skArc(sketch, "E79.19", {"start": v(-60, -40.3) * mm, "mid": v(-58.99, -44.68) * mm, "end": v(-56.15, -48.18) * mm});
            skLineSegment(sketch, "E80", {"start": v(0, -90) * mm, "end": v(0, -120) * mm, "construction": true});
            skPoint(sketch, "E80.endSnap0", {"position": v(0, -90) * mm});
            skLineSegment(sketch, "E81", {"start": v(33, -90) * mm, "end": v(15, -108) * mm});
            skLineSegment(sketch, "E82", {"start": v(15, -108) * mm, "end": v(15, -120) * mm});
            skLineSegment(sketch, "E83", {"start": v(-33, -90) * mm, "end": v(-15, -108) * mm});
            skLineSegment(sketch, "E84", {"start": v(-15, -108) * mm, "end": v(-15, -120) * mm});
            skArc(sketch, "E85", {"start": v(15, -120) * mm, "mid": v(0, -135) * mm, "end": v(-15, -120) * mm});
            skCircle(sketch, "E86", {"center": v(0, -120) * mm, "radius": 6 * mm});
            skLineSegment(sketch, "E87", {"start": v(80, 0) * mm, "end": v(-80, 0) * mm, "construction": true});
            skLineSegment(sketch, "E88.MirrorCS", {"start": v(0, 90) * mm, "end": v(0, 120) * mm, "construction": true});
            skLineSegment(sketch, "E89.MirrorCS", {"start": v(-15, 108) * mm, "end": v(-15, 120) * mm});
            skLineSegment(sketch, "E90.MirrorCS", {"start": v(15, 108) * mm, "end": v(15, 120) * mm});
            skPoint(sketch, "E91.MirrorP", {"position": v(0, 90) * mm});
            skLineSegment(sketch, "E92.MirrorCS", {"start": v(-33, 90) * mm, "end": v(-15, 108) * mm});
            skLineSegment(sketch, "E93.MirrorCS", {"start": v(33, 90) * mm, "end": v(15, 108) * mm});
            skArc(sketch, "E94.MirrorCS", {"start": v(15, 120) * mm, "mid": v(0, 135) * mm, "end": v(-15, 120) * mm});
            skCircle(sketch, "E95.MirrorC", {"center": v(0, 120) * mm, "radius": 6 * mm});
            skSolve(sketch);
        }
        {
            var Q0;
            Q0 = qSketchRegion(id + "F16", true);
            var Q1;
            Q1=makeQuery(id+"F2.opExtrude","CAP_FACE",FACE,{"disambiguationData":[OSD([sQuery(id+"F0.wireOp",EDGE,"E12"),sQuery(id+"F0.wireOp",EDGE,"E13"),sQuery(id+"F0.wireOp",EDGE,"E14"),sQuery(id+"F0.wireOp",EDGE,"E15"),sQuery(id+"F0.wireOp",EDGE,"E17.filletArc"),sQuery(id+"F0.wireOp",EDGE,"E18.filletArc"),sQuery(id+"F0.wireOp",EDGE,"E19.filletArc"),sQuery(id+"F0.wireOp",EDGE,"E20.filletArc"),sQuery(id+"F0.wireOp",EDGE,"E25.0"),sQuery(id+"F0.wireOp",EDGE,"E25.1"),sQuery(id+"F0.wireOp",EDGE,"E25.2"),sQuery(id+"F0.wireOp",EDGE,"E25.3"),sQuery(id+"F0.wireOp",EDGE,"E25.4"),sQuery(id+"F0.wireOp",EDGE,"E25.5"),sQuery(id+"F0.wireOp",EDGE,"E25.6"),sQuery(id+"F0.wireOp",EDGE,"E25.7")])],"isStart":false});
            extrude(context, id + "F17", {"entities" : qUnion([Q0]), "endBound" : BoundingType.UP_TO_SURFACE, "endBoundEntityFace" : qUnion([Q1]), "depth" : 25 * mm});
        }
    });
